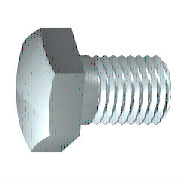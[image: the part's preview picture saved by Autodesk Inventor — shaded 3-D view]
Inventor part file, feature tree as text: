
AUTODESK INVENTOR PART (.ipt)
format: ipt  version: 2020 (Build 240168000, 168)  size: 194,560 bytes
history: native  units: mm (DEFAULTED — no unit token found)
features: sketch x3, extrude x1, chamfer x1, plane x1
ambient origin geometry x7: Origin, YZ Plane, XZ Plane, X Axis, Y Axis, Z Axis, Center Point
bodies: Solid1 (feature_tree), Body (feature_tree)
feature tree (6):
  extrude  "Head"  Depth=37.6mm
  chamfer  "Chamfer1"  Distance=3.0mm
  plane  "Work Plane1"
  sketch  "Sketch1"  dims[d0=40.0mm d1=37.6mm]
  sketch  "Sketch2"  dims[d2=5.0mm]
  sketch  "Sketch4"  dims[d12=90.0deg d3=3.0mm d4=0.0mm d5=30.0deg d21=90.0deg d6=0.49076mm d7=0.49086mm d8=0.0mm d9=0.5001mm d10=6.7mm d11=8.0mm d13=0.49086mm d14=4.566987mm d15=37.6mm d16=0.0mm d19=8.0mm d55=45.0deg d57=0.0mm d58=0.0mm]
